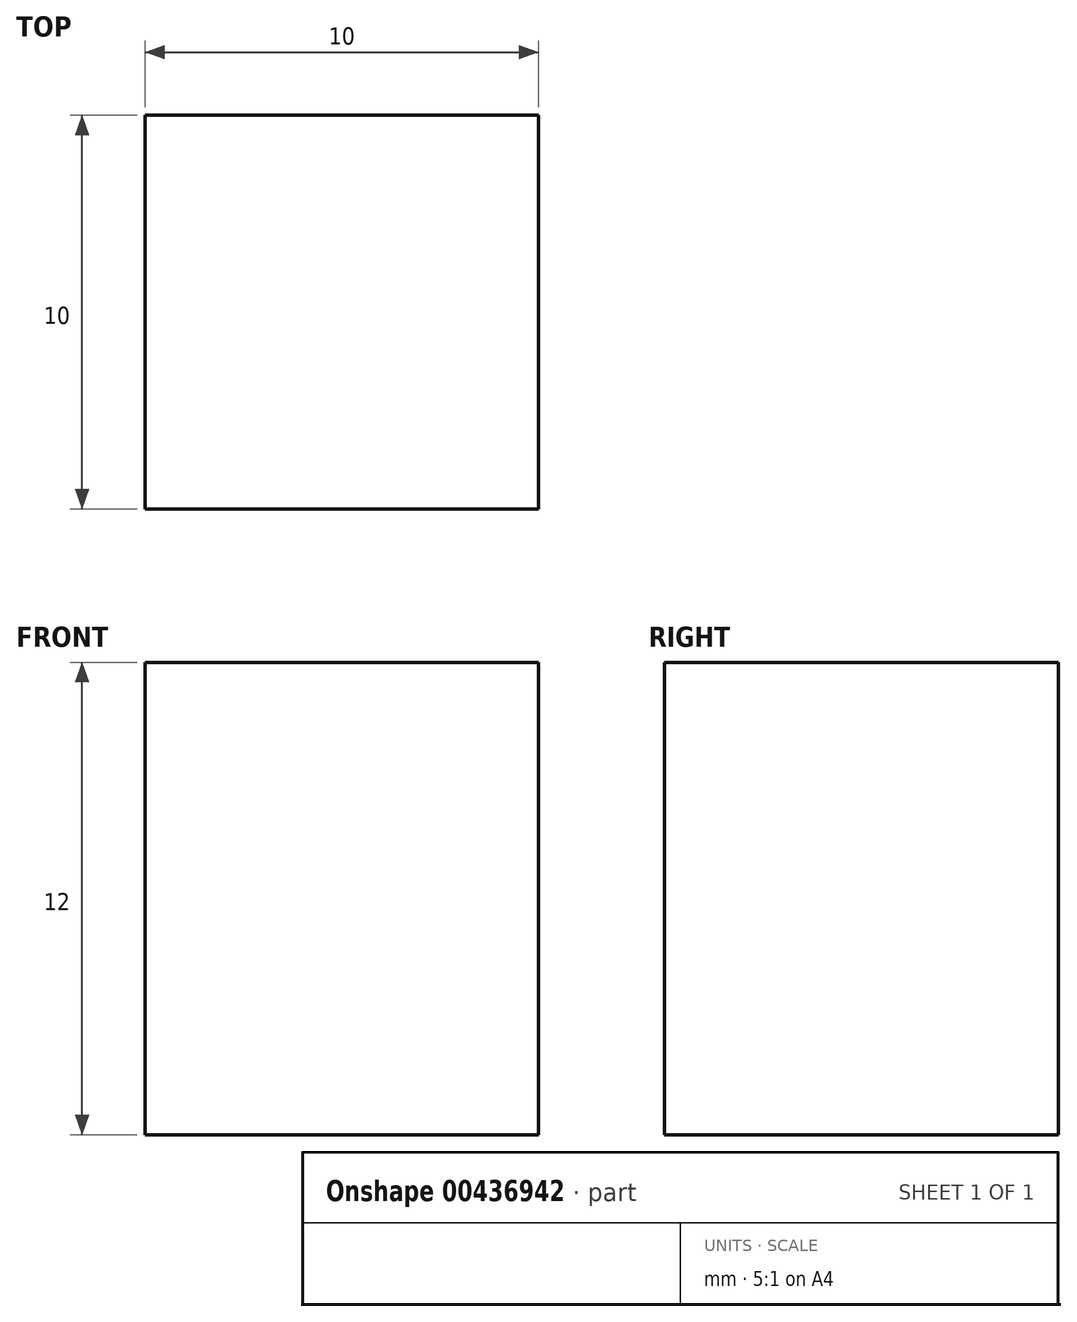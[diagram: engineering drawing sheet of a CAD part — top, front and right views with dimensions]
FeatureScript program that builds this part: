
annotation { "Feature Type Name" : "Feature", "Feature Type Description" : "" }
export const myFeature = defineFeature(function(context is Context, id is Id, definition is map)
    precondition{}
    {
        {
            var Q0;
            Q0=qCreatedBy(makeId("Front.planeOp"),FACE);
            var sketch = newSketch(context, id + "F0", { "sketchPlane" : qUnion([Q0])});
            skLineSegment(sketch, "E0.bottom", {"start": v(5, 6) * mm, "end": v(-5, 6) * mm});
            skLineSegment(sketch, "E0.top", {"start": v(5, -6) * mm, "end": v(-5, -6) * mm});
            skLineSegment(sketch, "E0.left", {"start": v(5, 6) * mm, "end": v(5, -6) * mm});
            skLineSegment(sketch, "E0.right", {"start": v(-5, 6) * mm, "end": v(-5, -6) * mm});
            skPoint(sketch, "E0.middle", {"position": v(0, 0) * mm});
            skSolve(sketch);
        }
        {
            var Q0;
            Q0 = qSketchRegion(id + "F0", true);
            extrude(context, id + "F1", {"entities" : qUnion([Q0]), "depth" : 10 * mm});
        }
    });
